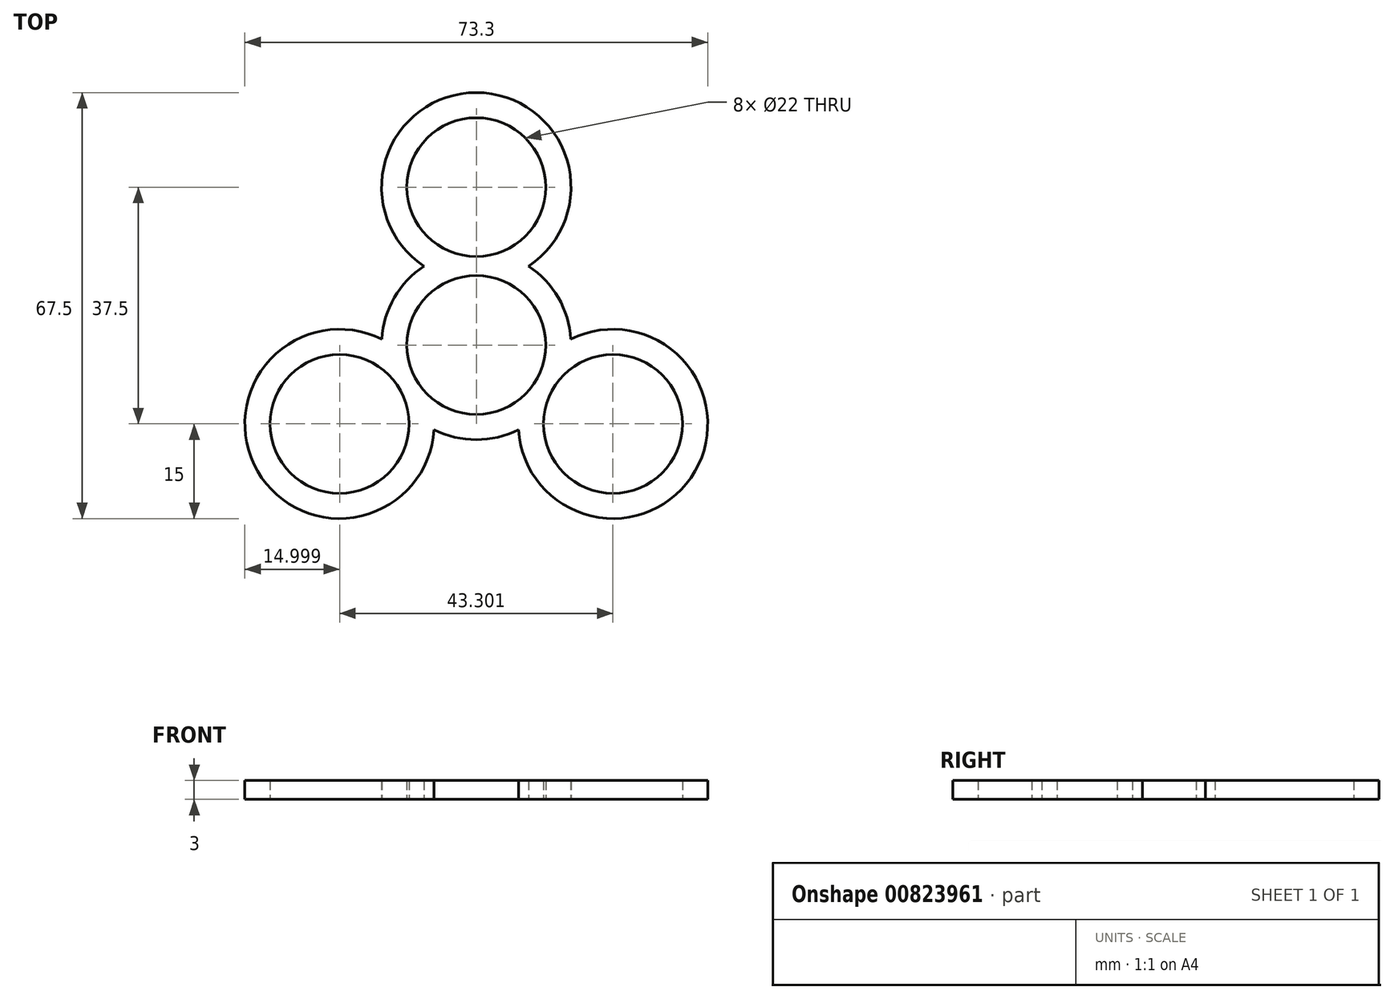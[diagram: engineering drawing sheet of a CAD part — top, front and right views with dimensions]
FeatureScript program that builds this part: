
annotation { "Feature Type Name" : "Feature", "Feature Type Description" : "" }
export const myFeature = defineFeature(function(context is Context, id is Id, definition is map)
    precondition{}
    {
        {
            var Q0;
            Q0=qCreatedBy(makeId("Top.planeOp"),FACE);
            var sketch = newSketch(context, id + "F0", { "sketchPlane" : qUnion([Q0])});
            skArc(sketch, "E0", {"start": v(9.53, 5.5) * mm, "mid": v(0, 11) * mm, "end": v(-9.53, 5.5) * mm});
            skCircle(sketch, "E1", {"center": v(0, 25) * mm, "radius": 11 * mm});
            skArc(sketch, "E2", {"start": v(13, 7.5) * mm, "mid": v(10.93, 10.27) * mm, "end": v(8.3, 12.5) * mm});
            skArc(sketch, "E3", {"start": v(8.3, 12.5) * mm, "mid": v(0, 40) * mm, "end": v(-8.3, 12.5) * mm});
            skArc(sketch, "E4.trimOffspring", {"start": v(-8.3, 12.5) * mm, "mid": v(-10.93, 10.27) * mm, "end": v(-13, 7.5) * mm});
            skCircle(sketch, "E5.1.0", {"center": v(-21.65, -12.5) * mm, "radius": 11 * mm});
            skArc(sketch, "E5.1.1", {"start": v(-14.97, 0.93) * mm, "mid": v(-34.64, -20) * mm, "end": v(-6.68, -13.43) * mm});
            skArc(sketch, "E5.1.2", {"start": v(-13, 7.5) * mm, "mid": v(-14.36, 4.33) * mm, "end": v(-14.97, 0.93) * mm});
            skArc(sketch, "E5.1.3", {"start": v(-9.53, 5.5) * mm, "mid": v(-9.53, -5.5) * mm, "end": v(0, -11) * mm});
            skArc(sketch, "E5.1.5", {"start": v(-6.68, -13.43) * mm, "mid": v(-3.43, -14.6) * mm, "end": v(0, -15) * mm});
            skCircle(sketch, "E5.2.0", {"center": v(21.65, -12.5) * mm, "radius": 11 * mm});
            skArc(sketch, "E5.2.1", {"start": v(6.68, -13.43) * mm, "mid": v(34.64, -20) * mm, "end": v(14.97, 0.93) * mm});
            skArc(sketch, "E5.2.2", {"start": v(0, -15) * mm, "mid": v(3.43, -14.6) * mm, "end": v(6.68, -13.43) * mm});
            skArc(sketch, "E5.2.3", {"start": v(0, -11) * mm, "mid": v(9.53, -5.5) * mm, "end": v(9.53, 5.5) * mm});
            skArc(sketch, "E5.2.5", {"start": v(14.97, 0.93) * mm, "mid": v(14.36, 4.33) * mm, "end": v(13, 7.5) * mm});
            skSolve(sketch);
        }
        {
            var Q0;
            Q0 = qSketchRegion(id + "F0", true);
            extrude(context, id + "F1", {"entities" : qUnion([Q0]), "depth" : 3 * mm, "offsetDistance" : 25 * mm});
        }
    });
